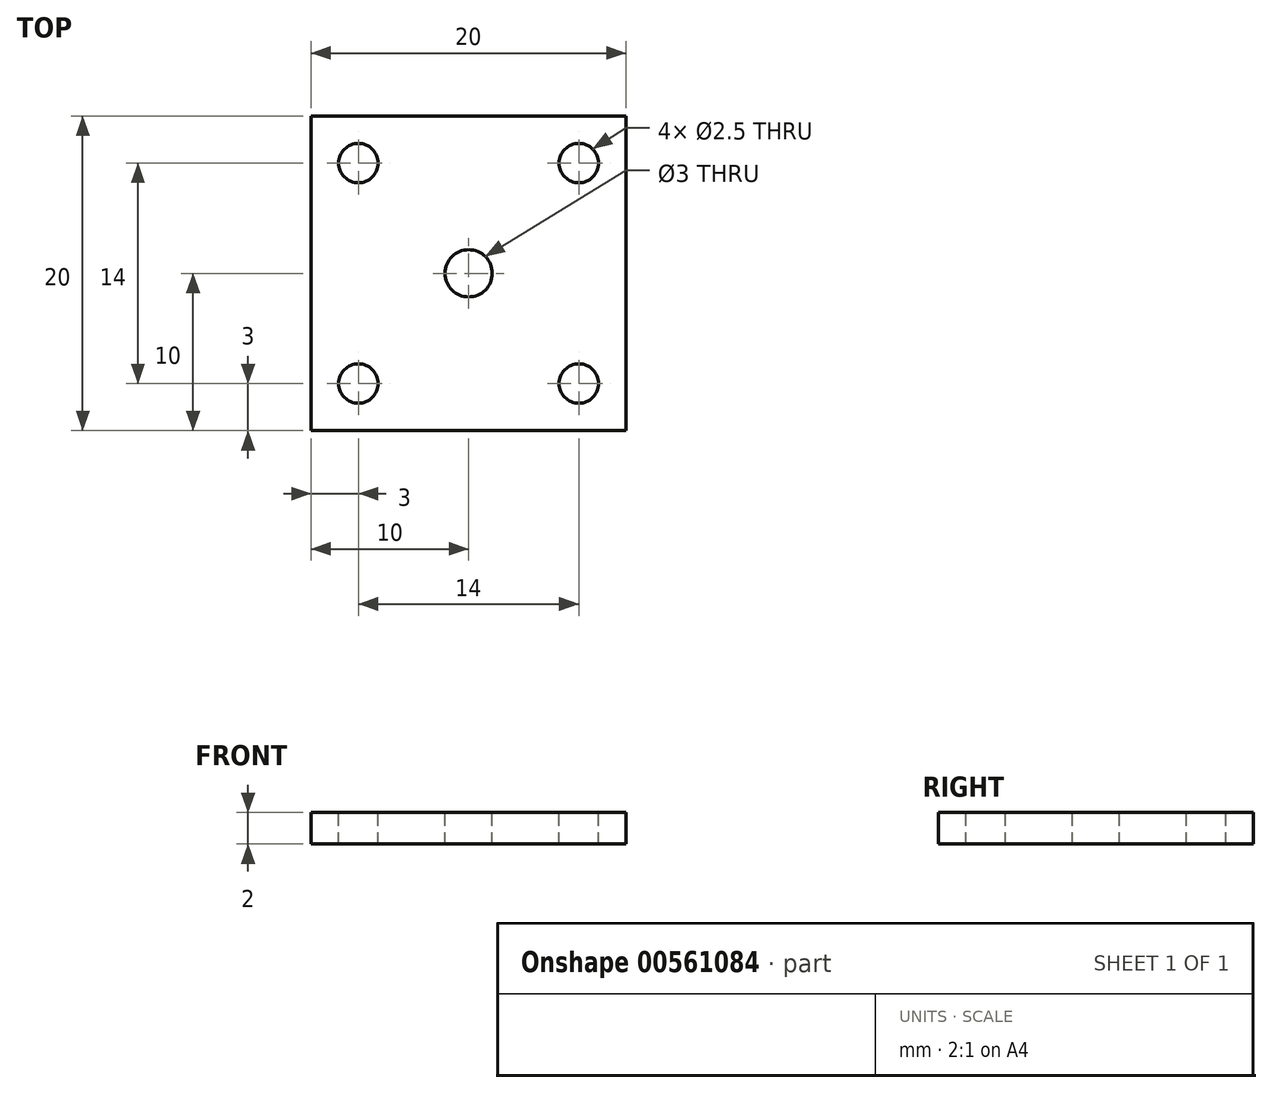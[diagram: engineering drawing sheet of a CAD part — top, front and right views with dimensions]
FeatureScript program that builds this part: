
annotation { "Feature Type Name" : "Feature", "Feature Type Description" : "" }
export const myFeature = defineFeature(function(context is Context, id is Id, definition is map)
    precondition{}
    {
        {
            var Q0;
            Q0=qCreatedBy(makeId("Top.planeOp"),FACE);
            var sketch = newSketch(context, id + "F0", { "sketchPlane" : qUnion([Q0])});
            skLineSegment(sketch, "E0.bottom", {"start": v(-10, 10) * mm, "end": v(10, 10) * mm});
            skLineSegment(sketch, "E0.top", {"start": v(-10, -10) * mm, "end": v(10, -10) * mm});
            skLineSegment(sketch, "E0.left", {"start": v(-10, 10) * mm, "end": v(-10, -10) * mm});
            skLineSegment(sketch, "E0.right", {"start": v(10, 10) * mm, "end": v(10, -10) * mm});
            skSolve(sketch);
        }
        {
            var Q0;
            Q0=makeQuery(id+"F0.imprint","IMPRINT",FACE,{"disambiguationData":[TD([[makeQuery(id+"F0.imprint","IMPRINT",EDGE,{"derivedFrom":sQuery(id+"F0.wireOp",EDGE,"E0.bottom")}),-1.0]])]});
            extrude(context, id + "F1", {"entities" : qUnion([Q0]), "oppositeDirection" : true, "depth" : 2 * mm, "offsetDistance" : 25 * mm});
        }
        {
            var Q0;
            Q0=makeQuery(id+"F1.opExtrude","CAP_FACE",FACE,{"disambiguationData":[OSD([sQuery(id+"F0.wireOp",EDGE,"E0.bottom"),sQuery(id+"F0.wireOp",EDGE,"E0.top"),sQuery(id+"F0.wireOp",EDGE,"E0.left"),sQuery(id+"F0.wireOp",EDGE,"E0.right")])],"isStart":true});
            var sketch = newSketch(context, id + "F2", { "sketchPlane" : qUnion([Q0])});
            skPoint(sketch, "E1", {"position": v(-7, 7) * mm});
            skPoint(sketch, "E2", {"position": v(7, 7) * mm});
            skLineSegment(sketch, "E3", {"start": v(-11.27, 0) * mm, "end": v(14.07, 0) * mm});
            skPoint(sketch, "E3.startSnap0", {"position": v(-10, 0) * mm});
            skPoint(sketch, "E3.endSnap0", {"position": v(10, 0) * mm});
            skPoint(sketch, "E4.MirrorP", {"position": v(-7, -7) * mm});
            skPoint(sketch, "E5.MirrorP", {"position": v(7, -7) * mm});
            skSolve(sketch);
        }
        {
            var Q0;
            Q0=sQuery(id+"F2.wireOp",VERTEX,"E1");
            var Q1;
            Q1=sQuery(id+"F2.wireOp",VERTEX,"E2");
            var Q2;
            Q2=sQuery(id+"F2.wireOp",VERTEX,"E4.MirrorP");
            var Q3;
            Q3=sQuery(id+"F2.wireOp",VERTEX,"E5.MirrorP");
            var Q4;
            Q4=makeQuery(id+"F1.opExtrude","SWEPT_BODY",BODY,{"disambiguationData":[OSD([sQuery(id+"F0.wireOp",EDGE,"E0.bottom"),sQuery(id+"F0.wireOp",EDGE,"E0.top"),sQuery(id+"F0.wireOp",EDGE,"E0.left"),sQuery(id+"F0.wireOp",EDGE,"E0.right")])]});
            hole(context, id + "F3", {"style" : HoleStyle.SIMPLE, "endStyle" : HoleEndStyle.THROUGH, "standardTappedOrClearance" : lookupTablePath({ "standard" : "ISO", "engagement" : "75%", "pitch" : "0.5 mm", "size" : "M3", "type" : "Tapped" }), "standardBlindInLast" : lookupTablePath({ "standard" : "ISO", "engagement" : "75%", "pitch" : "0.5 mm", "size" : "M3", "type" : "Tapped" }), "holeDiameter" : 2.5 * mm, "showTappedDepth" : true, "isTappedThrough" : true, "tappedDepth" : 12 * mm, "tapClearance" : 3, "startFromSketch" : true, "locations" : qUnion([Q0, Q1, Q2, Q3]), "scope" : qUnion([Q4]), "majorDiameter" : 3 * mm});
        }
        {
            var Q0;
            Q0=makeQuery(id+"F1.opExtrude","CAP_FACE",FACE,{"disambiguationData":[OSD([sQuery(id+"F0.wireOp",EDGE,"E0.bottom"),sQuery(id+"F0.wireOp",EDGE,"E0.top"),sQuery(id+"F0.wireOp",EDGE,"E0.left"),sQuery(id+"F0.wireOp",EDGE,"E0.right")])],"isStart":true});
            var sketch = newSketch(context, id + "F4", { "sketchPlane" : qUnion([Q0])});
            skCircle(sketch, "E6", {"center": v(0, 0) * mm, "radius": 1.5 * mm});
            skSolve(sketch);
        }
        {
            var Q0;
            Q0=makeQuery(id+"F4.imprint","IMPRINT",FACE,{"disambiguationData":[TD([[makeQuery(id+"F4.imprint","IMPRINT",EDGE,{"derivedFrom":sQuery(id+"F4.wireOp",EDGE,"E6")}),1.0]])]});
            extrude(context, id + "F5", {"entities" : qUnion([Q0]), "operationType" : NewBodyOperationType.REMOVE, "oppositeDirection" : true, "depth" : 25 * mm, "offsetDistance" : 25 * mm});
        }
    });
